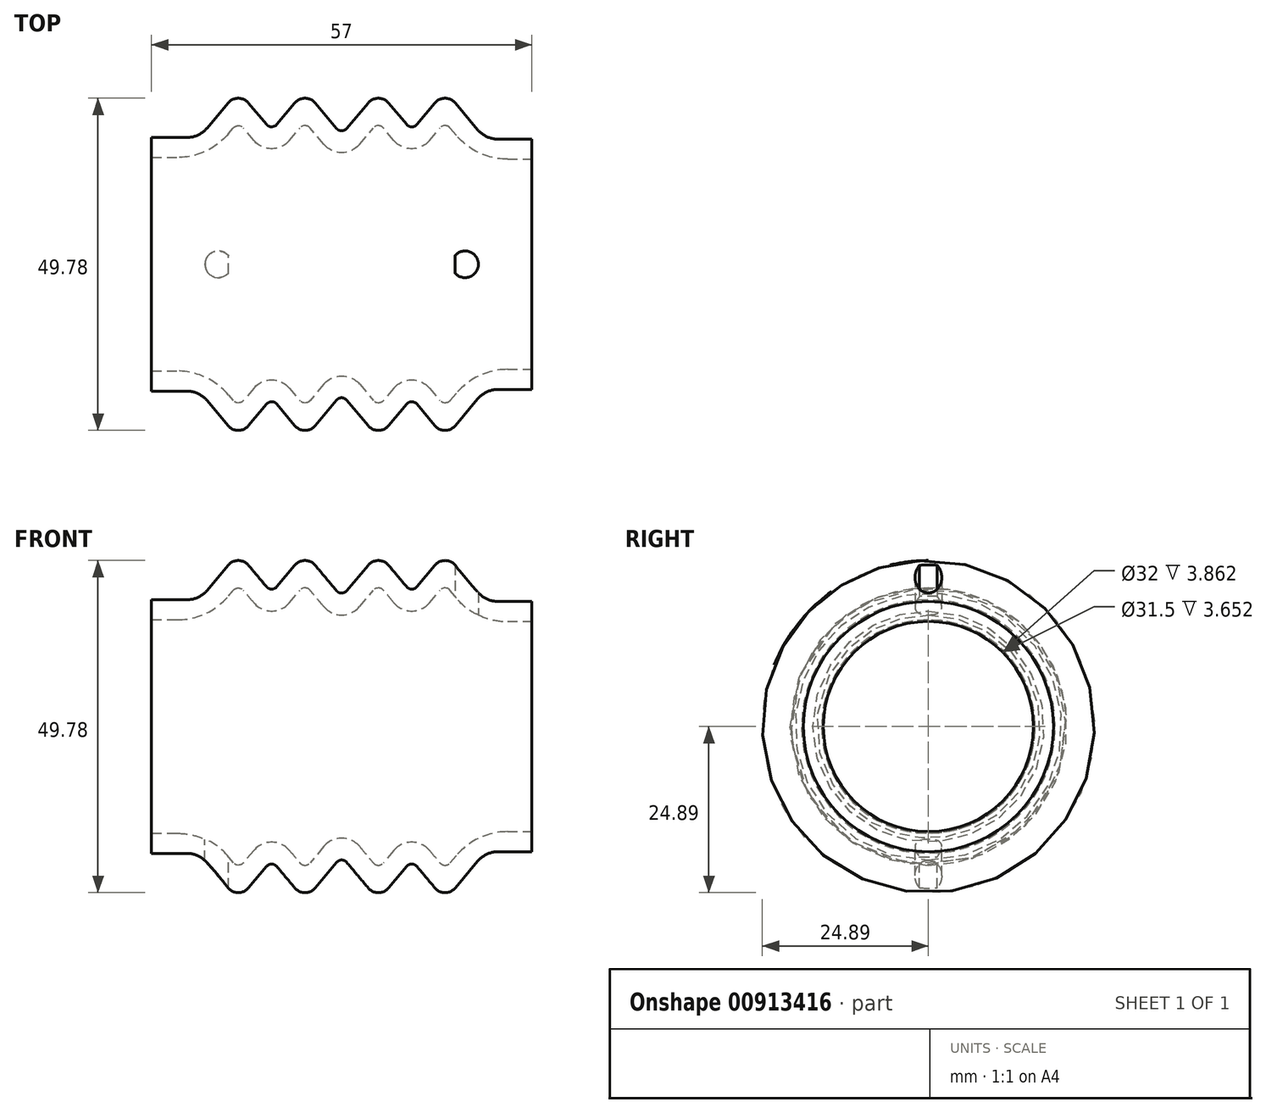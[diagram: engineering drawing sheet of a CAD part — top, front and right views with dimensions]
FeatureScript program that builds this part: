
annotation { "Feature Type Name" : "Feature", "Feature Type Description" : "" }
export const myFeature = defineFeature(function(context is Context, id is Id, definition is map)
    precondition{}
    {
        {
            var Q0;
            Q0=qCreatedBy(makeId("Front.planeOp"),FACE);
            var sketch = newSketch(context, id + "F0", { "sketchPlane" : qUnion([Q0])});
            skLineSegment(sketch, "E0", {"start": v(102.41, 0) * mm, "end": v(-38.11, 0) * mm, "construction": true});
            skLineSegment(sketch, "E1", {"start": v(0, 19) * mm, "end": v(0, 16) * mm});
            skLineSegment(sketch, "E2.0", {"start": v(57, 18.75) * mm, "end": v(57, 15.75) * mm});
            skLineSegment(sketch, "E3.0", {"start": v(57, 18.75) * mm, "end": v(50.08, 18.75) * mm});
            skLineSegment(sketch, "E4.0", {"start": v(7, 85.01) * mm, "end": v(7, -21.18) * mm, "construction": true});
            skLineSegment(sketch, "E5.0", {"start": v(50, 85.01) * mm, "end": v(50, -21.18) * mm, "construction": true});
            skLineSegment(sketch, "E6.trimOffspring", {"start": v(7.13, 19) * mm, "end": v(0, 19) * mm});
            skPoint(sketch, "E7.orphan", {"position": v(0, 85.01) * mm});
            skLineSegment(sketch, "E8.0", {"start": v(102.41, 26) * mm, "end": v(-38.11, 26) * mm, "construction": true});
            skLineSegment(sketch, "E9.0", {"start": v(13, 85.01) * mm, "end": v(13, -21.18) * mm, "construction": true});
            skLineSegment(sketch, "E10.0", {"start": v(44, 85.01) * mm, "end": v(44, -21.18) * mm, "construction": true});
            skLineSegment(sketch, "E11", {"start": v(13, 26) * mm, "end": v(7.13, 19) * mm});
            skLineSegment(sketch, "E12", {"start": v(13, 26) * mm, "end": v(18, 20.04) * mm});
            skLineSegment(sketch, "E13", {"start": v(44, 26) * mm, "end": v(50.08, 18.75) * mm});
            skLineSegment(sketch, "E14", {"start": v(44, 26) * mm, "end": v(39, 20.04) * mm});
            skLineSegment(sketch, "E15.0", {"start": v(34, 85.01) * mm, "end": v(34, -21.18) * mm, "construction": true});
            skLineSegment(sketch, "E16.0", {"start": v(23, 85.01) * mm, "end": v(23, -21.18) * mm, "construction": true});
            skLineSegment(sketch, "E17", {"start": v(23, 26) * mm, "end": v(18, 20.04) * mm});
            skLineSegment(sketch, "E18", {"start": v(23, 26) * mm, "end": v(28.5, 19.45) * mm});
            skLineSegment(sketch, "E19", {"start": v(34, 26) * mm, "end": v(28.5, 19.45) * mm});
            skLineSegment(sketch, "E20", {"start": v(34, 26) * mm, "end": v(39, 20.04) * mm});
            skLineSegment(sketch, "E21.1", {"start": v(8.53, 16) * mm, "end": v(0, 16) * mm});
            skLineSegment(sketch, "E21.2", {"start": v(44, 21.33) * mm, "end": v(39, 15.37) * mm});
            skLineSegment(sketch, "E21.3", {"start": v(44, 21.33) * mm, "end": v(48.68, 15.75) * mm});
            skLineSegment(sketch, "E21.4", {"start": v(57, 15.75) * mm, "end": v(48.68, 15.75) * mm});
            skLineSegment(sketch, "E21.6", {"start": v(34, 21.33) * mm, "end": v(39, 15.37) * mm});
            skLineSegment(sketch, "E21.7", {"start": v(34, 21.33) * mm, "end": v(28.5, 14.78) * mm});
            skLineSegment(sketch, "E21.8", {"start": v(23, 21.33) * mm, "end": v(28.5, 14.78) * mm});
            skLineSegment(sketch, "E21.9", {"start": v(23, 21.33) * mm, "end": v(18, 15.37) * mm});
            skLineSegment(sketch, "E21.10", {"start": v(13, 21.33) * mm, "end": v(18, 15.37) * mm});
            skLineSegment(sketch, "E21.11", {"start": v(13, 21.33) * mm, "end": v(8.53, 16) * mm});
            skSolve(sketch);
        }
        {
            var Q0;
            Q0=makeQuery(id+"F0.imprint","IMPRINT",FACE,{"disambiguationData":[TD([[makeQuery(id+"F0.imprint","IMPRINT",EDGE,{"derivedFrom":sQuery(id+"F0.wireOp",EDGE,"E1")}),1.0]])]});
            var Q1;
            Q1=sQuery(id+"F0.wireOp",EDGE,"E0");
            revolve(context, id + "F1", {"surfaceOperationType" : NewSurfaceOperationType.NEW, "entities" : qUnion([Q0]), "axis" : qUnion([Q1]), "revolveType" : RevolveType.FULL});
        }
        {
            var Q0;
            Q0=makeQuery(id+"F1.opRevolve","SWEPT_EDGE",EDGE,{"disambiguationData":[OSD([sQuery(id+"F0.wireOp",EDGE,"E11"),sQuery(id+"F0.wireOp",EDGE,"E12")])]});
            var Q1;
            Q1=makeQuery(id+"F1.opRevolve","SWEPT_EDGE",EDGE,{"disambiguationData":[OSD([sQuery(id+"F0.wireOp",EDGE,"E17"),sQuery(id+"F0.wireOp",EDGE,"E18")])]});
            var Q2;
            Q2=makeQuery(id+"F1.opRevolve","SWEPT_EDGE",EDGE,{"disambiguationData":[OSD([sQuery(id+"F0.wireOp",EDGE,"E19"),sQuery(id+"F0.wireOp",EDGE,"E20")])]});
            var Q3;
            Q3=makeQuery(id+"F1.opRevolve","SWEPT_EDGE",EDGE,{"disambiguationData":[OSD([sQuery(id+"F0.wireOp",EDGE,"E13"),sQuery(id+"F0.wireOp",EDGE,"E14")])]});
            fillet(context, id + "F2", {"entities" : qUnion([Q0, Q1, Q2, Q3]), "radius" : 2 * mm, "tangentPropagation" : true, "allowEdgeOverflow" : false});
        }
        {
            var Q0;
            Q0=makeQuery(id+"F1.opRevolve","SWEPT_EDGE",EDGE,{"disambiguationData":[OSD([sQuery(id+"F0.wireOp",EDGE,"E21.10"),sQuery(id+"F0.wireOp",EDGE,"E21.11")])]});
            var Q1;
            Q1=makeQuery(id+"F1.opRevolve","SWEPT_EDGE",EDGE,{"disambiguationData":[OSD([sQuery(id+"F0.wireOp",EDGE,"E21.8"),sQuery(id+"F0.wireOp",EDGE,"E21.9")])]});
            var Q2;
            Q2=makeQuery(id+"F1.opRevolve","SWEPT_EDGE",EDGE,{"disambiguationData":[OSD([sQuery(id+"F0.wireOp",EDGE,"E21.6"),sQuery(id+"F0.wireOp",EDGE,"E21.7")])]});
            var Q3;
            Q3=makeQuery(id+"F1.opRevolve","SWEPT_EDGE",EDGE,{"disambiguationData":[OSD([sQuery(id+"F0.wireOp",EDGE,"E21.2"),sQuery(id+"F0.wireOp",EDGE,"E21.3")])]});
            fillet(context, id + "F3", {"entities" : qUnion([Q0, Q1, Q2, Q3]), "radius" : 1 * mm, "tangentPropagation" : true, "allowEdgeOverflow" : false});
        }
        {
            var Q0;
            Q0=makeQuery(id+"F1.opRevolve","SWEPT_EDGE",EDGE,{"disambiguationData":[OSD([sQuery(id+"F0.wireOp",EDGE,"E21.1"),sQuery(id+"F0.wireOp",EDGE,"E21.11")])]});
            var Q1;
            Q1=makeQuery(id+"F1.opRevolve","SWEPT_EDGE",EDGE,{"disambiguationData":[OSD([sQuery(id+"F0.wireOp",EDGE,"E21.3"),sQuery(id+"F0.wireOp",EDGE,"E21.4")])]});
            fillet(context, id + "F4", {"entities" : qUnion([Q0, Q1]), "radius" : 10 * mm, "tangentPropagation" : true, "allowEdgeOverflow" : false});
        }
        {
            var Q0;
            Q0=makeQuery(id+"F1.opRevolve","SWEPT_EDGE",EDGE,{"disambiguationData":[OSD([sQuery(id+"F0.wireOp",EDGE,"E3.0"),sQuery(id+"F0.wireOp",EDGE,"E13")])]});
            var Q1;
            Q1=makeQuery(id+"F1.opRevolve","SWEPT_EDGE",EDGE,{"disambiguationData":[OSD([sQuery(id+"F0.wireOp",EDGE,"E6.trimOffspring"),sQuery(id+"F0.wireOp",EDGE,"E11")])]});
            fillet(context, id + "F5", {"entities" : qUnion([Q0, Q1]), "radius" : 4 * mm, "tangentPropagation" : true, "allowEdgeOverflow" : false});
        }
        {
            var Q0;
            Q0=makeQuery(id+"F1.opRevolve","SWEPT_EDGE",EDGE,{"disambiguationData":[OSD([sQuery(id+"F0.wireOp",EDGE,"E21.9"),sQuery(id+"F0.wireOp",EDGE,"E21.10")])]});
            var Q1;
            Q1=makeQuery(id+"F1.opRevolve","SWEPT_EDGE",EDGE,{"disambiguationData":[OSD([sQuery(id+"F0.wireOp",EDGE,"E21.7"),sQuery(id+"F0.wireOp",EDGE,"E21.8")])]});
            var Q2;
            Q2=makeQuery(id+"F1.opRevolve","SWEPT_EDGE",EDGE,{"disambiguationData":[OSD([sQuery(id+"F0.wireOp",EDGE,"E21.2"),sQuery(id+"F0.wireOp",EDGE,"E21.6")])]});
            fillet(context, id + "F6", {"entities" : qUnion([Q0, Q1, Q2]), "radius" : 3.5 * mm, "tangentPropagation" : true, "allowEdgeOverflow" : false});
        }
        {
            var Q0;
            Q0=makeQuery(id+"F1.opRevolve","SWEPT_EDGE",EDGE,{"disambiguationData":[OSD([sQuery(id+"F0.wireOp",EDGE,"E12"),sQuery(id+"F0.wireOp",EDGE,"E17")])]});
            var Q1;
            Q1=makeQuery(id+"F1.opRevolve","SWEPT_EDGE",EDGE,{"disambiguationData":[OSD([sQuery(id+"F0.wireOp",EDGE,"E18"),sQuery(id+"F0.wireOp",EDGE,"E19")])]});
            var Q2;
            Q2=makeQuery(id+"F1.opRevolve","SWEPT_EDGE",EDGE,{"disambiguationData":[OSD([sQuery(id+"F0.wireOp",EDGE,"E14"),sQuery(id+"F0.wireOp",EDGE,"E20")])]});
            fillet(context, id + "F7", {"entities" : qUnion([Q0, Q1, Q2]), "radius" : 1 * mm, "tangentPropagation" : true, "allowEdgeOverflow" : false});
        }
        {
            var Q0;
            Q0=qCreatedBy(makeId("Top.planeOp"),FACE);
            var sketch = newSketch(context, id + "F8", { "sketchPlane" : qUnion([Q0])});
            skLineSegment(sketch, "E22", {"start": v(0, 18.4) * mm, "end": v(0, -14.41) * mm, "construction": true});
            skLineSegment(sketch, "E23", {"start": v(-5.08, 0) * mm, "end": v(82.37, 0) * mm, "construction": true});
            skLineSegment(sketch, "E24.0", {"start": v(10, 18.4) * mm, "end": v(10, -14.41) * mm, "construction": true});
            skLineSegment(sketch, "E25.0", {"start": v(57, 18.4) * mm, "end": v(57, -14.41) * mm});
            skLineSegment(sketch, "E26.0", {"start": v(47, 18.4) * mm, "end": v(47, -14.41) * mm});
            skArc(sketch, "E27", {"start": v(11.5, 1.32) * mm, "mid": v(8, 0) * mm, "end": v(11.5, -1.32) * mm});
            skLineSegment(sketch, "E28.0", {"start": v(11.5, 1.32) * mm, "end": v(11.5, -1.32) * mm});
            skLineSegment(sketch, "E29.0", {"start": v(28.5, 18.4) * mm, "end": v(28.5, -14.41) * mm, "construction": true});
            skLineSegment(sketch, "E30.MirrorCS", {"start": v(45.5, 1.32) * mm, "end": v(45.5, -1.32) * mm});
            skArc(sketch, "E31.MirrorCS", {"start": v(45.5, 1.32) * mm, "mid": v(49, 0) * mm, "end": v(45.5, -1.32) * mm});
            skSolve(sketch);
        }
        {
            var Q0;
            Q0=makeQuery(id+"F8.imprint","IMPRINT",FACE,{"disambiguationData":[TD([[makeQuery(id+"F8.imprint","IMPRINT",EDGE,{"derivedFrom":sQuery(id+"F8.wireOp",EDGE,"E27")}),1.0]])]});
            extrude(context, id + "F9", {"entities" : qUnion([Q0]), "operationType" : NewBodyOperationType.REMOVE, "oppositeDirection" : true, "depth" : 50 * mm, "offsetDistance" : 25 * mm});
        }
        {
            var Q0;
            {var subQ0=sQuery(id+"F8.wireOp",EDGE,"E31.MirrorCS");var subQ1=sQuery(id+"F8.wireOp",EDGE,"E26.0");var subQ2=makeQuery(id+"F8.imprint","INTERSECT",VERTEX,{"disambiguationData":[OD(0.0)],"derivedFrom":[subQ1,subQ0]});Q0=makeQuery(id+"F8.imprint","IMPRINT",FACE,{"disambiguationData":[TD([[makeQuery(id+"F8.imprint","IMPRINT",EDGE,{"disambiguationData":[TD([[subQ2,-1.0]])],"derivedFrom":subQ1}),1.0]])]});}
            var Q1;
            {var subQ4=sQuery(id+"F8.wireOp",EDGE,"E30.MirrorCS");Q1=makeQuery(id+"F8.imprint","IMPRINT",FACE,{"disambiguationData":[TD([[makeQuery(id+"F8.imprint","IMPRINT",EDGE,{"derivedFrom":subQ4}),1.0]])]});}
            extrude(context, id + "F10", {"entities" : qUnion([Q0, Q1]), "operationType" : NewBodyOperationType.REMOVE, "depth" : 50 * mm, "offsetDistance" : 25 * mm});
        }
    });
